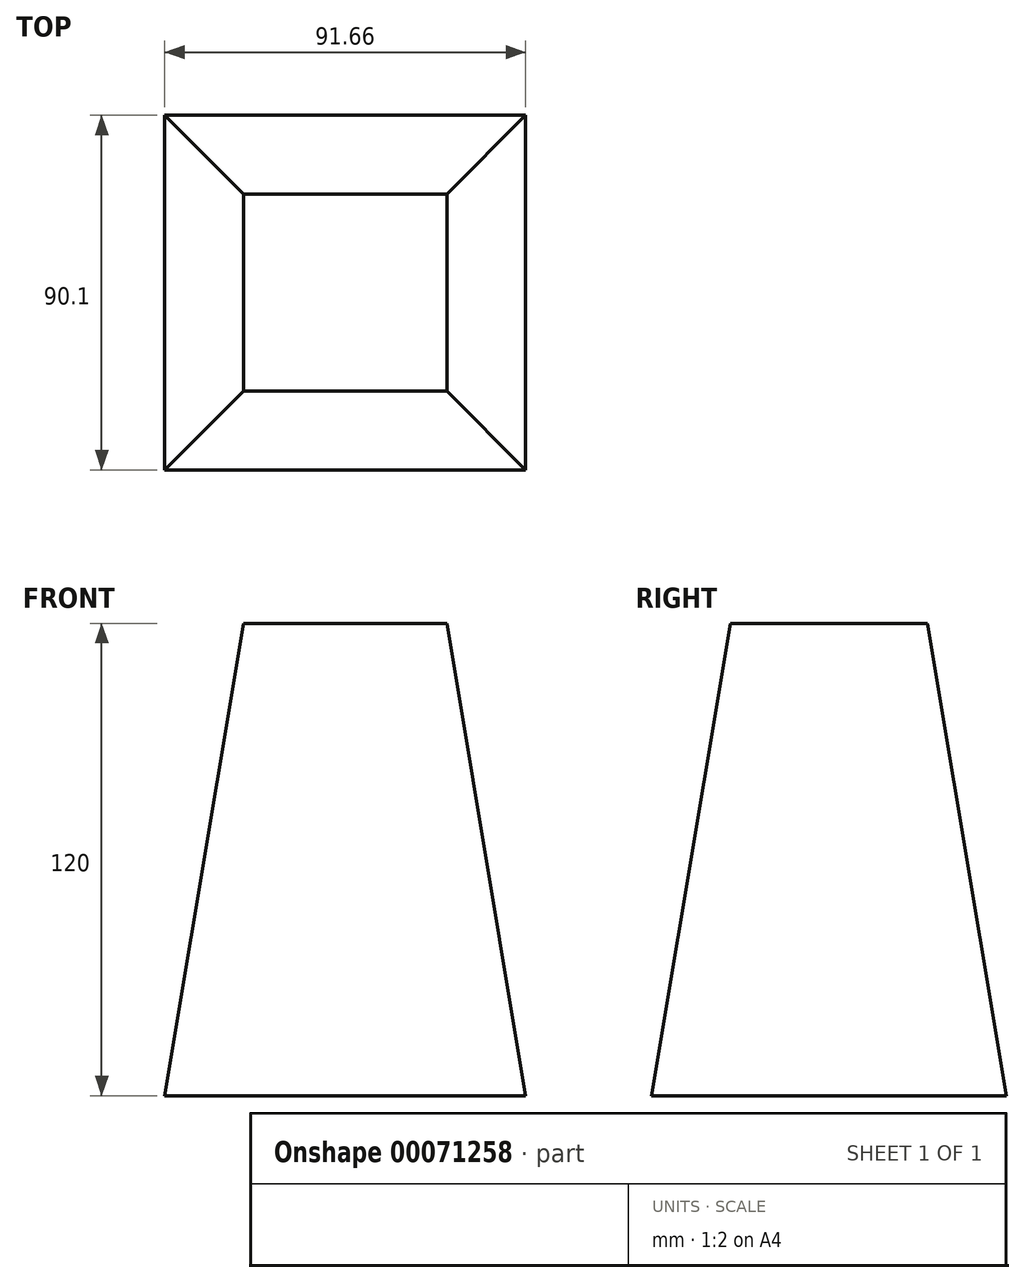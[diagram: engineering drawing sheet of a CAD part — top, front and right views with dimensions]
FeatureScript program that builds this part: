
annotation { "Feature Type Name" : "Feature", "Feature Type Description" : "" }
export const myFeature = defineFeature(function(context is Context, id is Id, definition is map)
    precondition{}
    {
        {
            var Q0;
            Q0=qCreatedBy(makeId("Top.planeOp"),FACE);
            var sketch = newSketch(context, id + "F0", { "sketchPlane" : qUnion([Q0])});
            skLineSegment(sketch, "E0.rect.bottom", {"start": v(35.83, -35.05) * mm, "end": v(-35.83, -35.05) * mm});
            skLineSegment(sketch, "E0.rect.top", {"start": v(35.83, 35.05) * mm, "end": v(-35.83, 35.05) * mm});
            skLineSegment(sketch, "E0.rect.left", {"start": v(35.83, -35.05) * mm, "end": v(35.83, 35.05) * mm});
            skLineSegment(sketch, "E0.rect.right", {"start": v(-35.83, -35.05) * mm, "end": v(-35.83, 35.05) * mm});
            skPoint(sketch, "E0.rect.middle", {"position": v(0, 0) * mm});
            skSolve(sketch);
        }
        {
            var Q0;
            Q0=qCreatedBy(makeId("Top.planeOp"),FACE);
            cPlane(context, id + "F1", {"entities" : qUnion([Q0]), "cplaneType" : CPlaneType.OFFSET, "offset" : 60 * mm, "width" : 150 * mm, "height" : 150 * mm});
        }
        {
            var Q0;
            Q0=qCreatedBy(makeId("Top.planeOp"),FACE);
            cPlane(context, id + "F2", {"entities" : qUnion([Q0]), "cplaneType" : CPlaneType.OFFSET, "offset" : 60 * mm, "oppositeDirection" : true, "width" : 150 * mm, "height" : 150 * mm});
        }
        {
            var Q0;
            Q0=qCreatedBy(id+"F1.planeOp",FACE);
            var sketch = newSketch(context, id + "F3", { "sketchPlane" : qUnion([Q0])});
            skLineSegment(sketch, "E1.0", {"start": v(25.83, 25.05) * mm, "end": v(-25.83, 25.05) * mm});
            skLineSegment(sketch, "E1.1", {"start": v(25.83, -25.05) * mm, "end": v(25.83, 25.05) * mm});
            skLineSegment(sketch, "E1.2", {"start": v(25.83, -25.05) * mm, "end": v(-25.83, -25.05) * mm});
            skLineSegment(sketch, "E1.3", {"start": v(-25.83, -25.05) * mm, "end": v(-25.83, 25.05) * mm});
            skSolve(sketch);
        }
        {
            var Q0;
            Q0=qCreatedBy(id+"F2.planeOp",FACE);
            var sketch = newSketch(context, id + "F4", { "sketchPlane" : qUnion([Q0])});
            skLineSegment(sketch, "E2.0", {"start": v(45.83, 45.05) * mm, "end": v(-45.83, 45.05) * mm});
            skLineSegment(sketch, "E2.1", {"start": v(45.83, -45.05) * mm, "end": v(45.83, 45.05) * mm});
            skLineSegment(sketch, "E2.2", {"start": v(45.83, -45.05) * mm, "end": v(-45.83, -45.05) * mm});
            skLineSegment(sketch, "E2.3", {"start": v(-45.83, -45.05) * mm, "end": v(-45.83, 45.05) * mm});
            skSolve(sketch);
        }
        {
            var Q0;
            Q0=makeQuery(id+"F4.imprint","IMPRINT",FACE,{"disambiguationData":[TD([[makeQuery(id+"F4.imprint","IMPRINT",EDGE,{"derivedFrom":sQuery(id+"F4.wireOp",EDGE,"E2.0")}),1.0]])]});
            var Q1;
            Q1=makeQuery(id+"F0.imprint","IMPRINT",FACE,{"disambiguationData":[TD([[makeQuery(id+"F0.imprint","IMPRINT",EDGE,{"derivedFrom":sQuery(id+"F0.wireOp",EDGE,"E0.rect.bottom")}),-1.0]])]});
            loft(context, id + "F5", {"sheetProfilesArray" : [{ "sheetProfileEntities" : qUnion([Q0]) }, { "sheetProfileEntities" : qUnion([Q1]) }]});
        }
        {
            var Q1;
            Q1=makeQuery(id+"F5.opLoft","CAP_FACE",FACE,{"disambiguationData":[OSD([makeQuery(id+"F0.imprint","IMPRINT",FACE,{"disambiguationData":[TD([[makeQuery(id+"F0.imprint","IMPRINT",EDGE,{"derivedFrom":sQuery(id+"F0.wireOp",EDGE,"E0.rect.bottom")}),-1.0]])]})])],"isStart":true});
            var Q2;
            Q2=makeQuery(id+"F3.imprint","IMPRINT",FACE,{"disambiguationData":[TD([[makeQuery(id+"F3.imprint","IMPRINT",EDGE,{"derivedFrom":sQuery(id+"F3.wireOp",EDGE,"E1.0")}),1.0]])]});
            loft(context, id + "F6", {"operationType" : NewBodyOperationType.ADD, "sheetProfilesArray" : [{ "sheetProfileEntities" : qUnion([Q1]) }, { "sheetProfileEntities" : qUnion([Q2]) }]});
        }
    });
